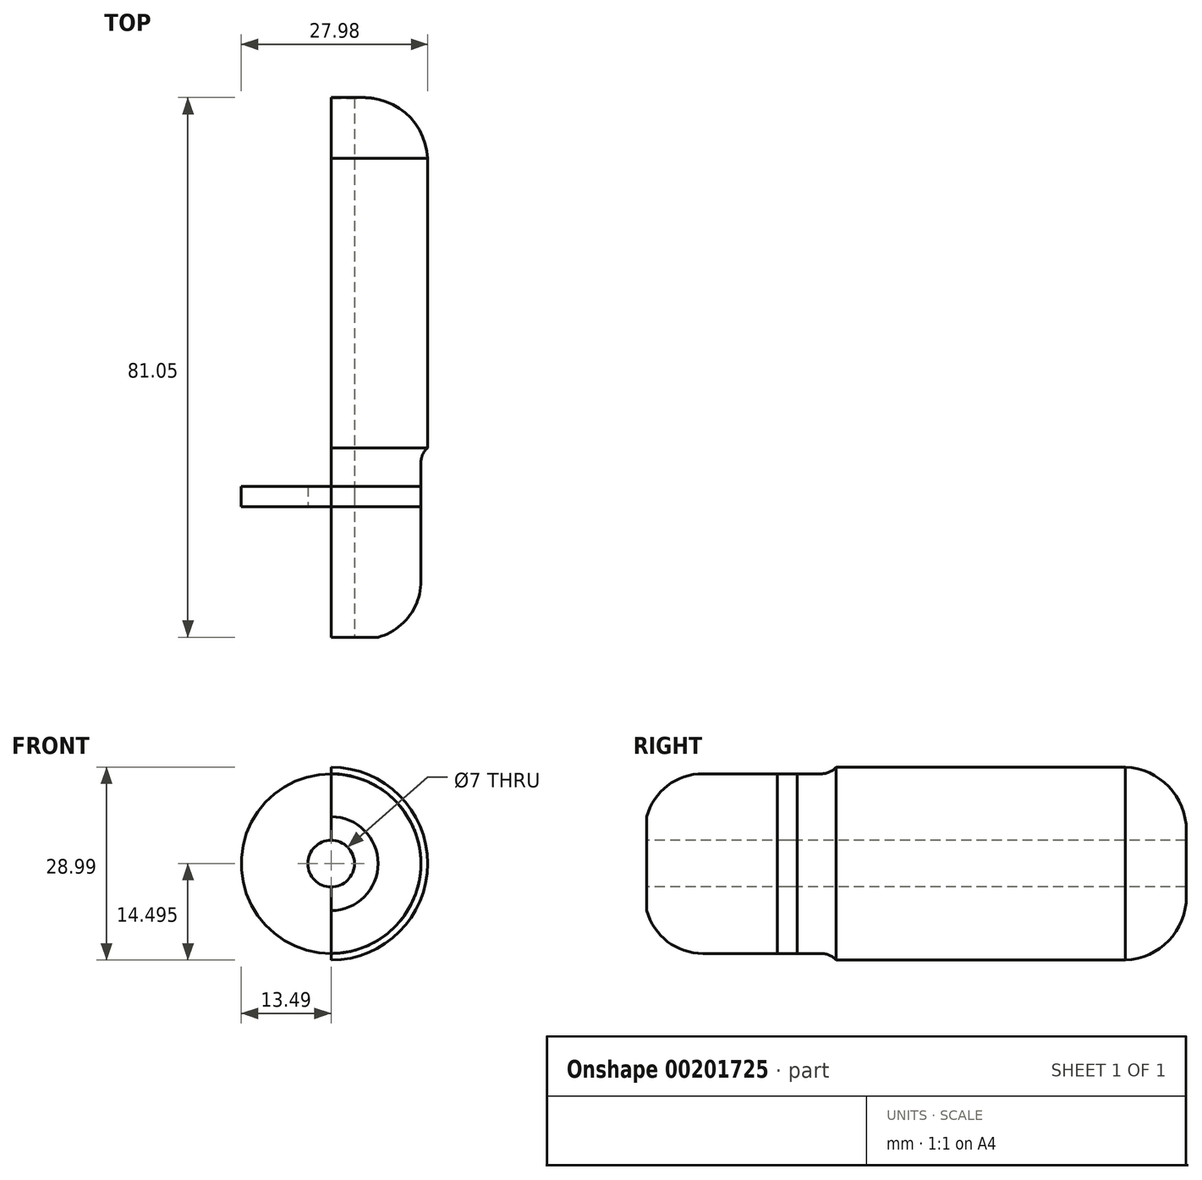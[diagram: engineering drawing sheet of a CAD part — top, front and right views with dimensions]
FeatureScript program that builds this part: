
annotation { "Feature Type Name" : "Feature", "Feature Type Description" : "" }
export const myFeature = defineFeature(function(context is Context, id is Id, definition is map)
    precondition{}
    {
        {
            var Q0;
            Q0=qCreatedBy(makeId("Right.planeOp"),FACE);
            var sketch = newSketch(context, id + "F0", { "sketchPlane" : qUnion([Q0])});
            skLineSegment(sketch, "E0.bottom", {"start": v(-3.13, 33.38) * mm, "end": v(86.87, 33.38) * mm});
            skLineSegment(sketch, "E0.top", {"start": v(-3.13, 32.38) * mm, "end": v(4.08, 32.38) * mm});
            skLineSegment(sketch, "E0.left", {"start": v(-3.13, 33.38) * mm, "end": v(-3.13, 32.38) * mm});
            skLineSegment(sketch, "E0.right", {"start": v(86.87, 33.38) * mm, "end": v(86.87, 32.38) * mm});
            skPoint(sketch, "E0.middle", {"position": v(41.87, 32.88) * mm});
            skLineSegment(sketch, "E1.bottom", {"start": v(86.87, 32.38) * mm, "end": v(81.87, 32.38) * mm, "construction": true});
            skLineSegment(sketch, "E1.top", {"start": v(86.87, 21.38) * mm, "end": v(85.87, 21.38) * mm});
            skLineSegment(sketch, "E1.left", {"start": v(86.87, 32.38) * mm, "end": v(86.87, 21.38) * mm, "construction": true});
            skLineSegment(sketch, "E1.right", {"start": v(81.87, 32.38) * mm, "end": v(81.87, 21.38) * mm, "construction": true});
            skLineSegment(sketch, "E2.bottom", {"start": v(81.87, 32.38) * mm, "end": v(71.87, 32.38) * mm, "construction": true});
            skLineSegment(sketch, "E2.top", {"start": v(81.87, 21.38) * mm, "end": v(71.87, 21.38) * mm, "construction": true});
            skLineSegment(sketch, "E2.right", {"start": v(71.87, 33.38) * mm, "end": v(71.87, 21.38) * mm, "construction": true});
            skLineSegment(sketch, "E3.0", {"start": v(85.87, 22.38) * mm, "end": v(85.37, 22.38) * mm, "construction": true});
            skLineSegment(sketch, "E4.0", {"start": v(85.87, 32.38) * mm, "end": v(85.87, 21.38) * mm, "construction": true});
            skArc(sketch, "E5", {"start": v(82.3, 22.38) * mm, "mid": v(80.84, 28.3) * mm, "end": v(76.33, 32.38) * mm});
            skArc(sketch, "E6", {"start": v(81.87, 21.38) * mm, "mid": v(79.3, 29.1) * mm, "end": v(71.87, 32.38) * mm});
            skLineSegment(sketch, "E7.trimOffspring", {"start": v(76.33, 32.38) * mm, "end": v(86.87, 32.38) * mm});
            skLineSegment(sketch, "E8.top", {"start": v(86.87, 25.38) * mm, "end": v(85.87, 25.38) * mm});
            skLineSegment(sketch, "E8.left", {"start": v(86.87, 23.38) * mm, "end": v(86.87, 25.38) * mm});
            skLineSegment(sketch, "E8.right", {"start": v(85.87, 22.38) * mm, "end": v(85.87, 22.72) * mm, "construction": true});
            skLineSegment(sketch, "E9.bottom", {"start": v(-3.13, 32.38) * mm, "end": v(-2.13, 32.38) * mm, "construction": true});
            skLineSegment(sketch, "E9.top", {"start": v(-3.13, 21.38) * mm, "end": v(-2.13, 21.38) * mm});
            skLineSegment(sketch, "E9.left", {"start": v(-3.13, 32.38) * mm, "end": v(-3.13, 21.38) * mm, "construction": true});
            skLineSegment(sketch, "E9.right", {"start": v(-2.13, 32.38) * mm, "end": v(-2.13, 21.38) * mm, "construction": true});
            skLineSegment(sketch, "E10.bottom", {"start": v(-2.13, 32.38) * mm, "end": v(4.08, 32.38) * mm, "construction": true});
            skLineSegment(sketch, "E10.top", {"start": v(-2.13, 33.38) * mm, "end": v(8.87, 33.38) * mm, "construction": true});
            skLineSegment(sketch, "E10.left", {"start": v(-2.13, 32.38) * mm, "end": v(-2.13, 33.38) * mm, "construction": true});
            skLineSegment(sketch, "E10.right", {"start": v(8.87, 32.38) * mm, "end": v(8.87, 33.38) * mm, "construction": true});
            skArc(sketch, "E11", {"start": v(4.08, 32.38) * mm, "mid": v(-1.17, 27.96) * mm, "end": v(-3.13, 21.38) * mm});
            skArc(sketch, "E12", {"start": v(8.87, 32.38) * mm, "mid": v(1.1, 29.16) * mm, "end": v(-2.13, 21.38) * mm});
            skLineSegment(sketch, "E13.trimOffspring", {"start": v(8.87, 32.38) * mm, "end": v(71.87, 32.38) * mm});
            skLineSegment(sketch, "E14", {"start": v(8.87, 21.38) * mm, "end": v(71.87, 21.38) * mm, "construction": true});
            skLineSegment(sketch, "E15.0", {"start": v(8.87, 17.38) * mm, "end": v(71.87, 17.38) * mm, "construction": true});
            skLineSegment(sketch, "E16.0", {"start": v(86.87, 23.38) * mm, "end": v(85.87, 23.38) * mm, "construction": true});
            skLineSegment(sketch, "E17.0", {"start": v(83.87, 21.38) * mm, "end": v(83.87, 25.38) * mm, "construction": true});
            skLineSegment(sketch, "E18", {"start": v(86.87, 23.38) * mm, "end": v(83.87, 21.38) * mm});
            skLineSegment(sketch, "E19.0", {"start": v(85.87, 23.92) * mm, "end": v(83.57, 22.38) * mm});
            skLineSegment(sketch, "E20.trimOffspring", {"start": v(83.87, 21.38) * mm, "end": v(81.87, 21.38) * mm});
            skLineSegment(sketch, "E21.trimOffspring", {"start": v(83.57, 22.38) * mm, "end": v(82.3, 22.38) * mm});
            skLineSegment(sketch, "E22.trimOffspring", {"start": v(85.87, 23.92) * mm, "end": v(85.87, 25.38) * mm});
            skSolve(sketch);
        }
        {
            var Q0;
            Q0=qCreatedBy(makeId("Right.planeOp"),FACE);
            var sketch = newSketch(context, id + "F1", { "sketchPlane" : qUnion([Q0])});
            skLineSegment(sketch, "E23.bottom", {"start": v(-3.13, 33.38) * mm, "end": v(28.58, 33.38) * mm, "construction": true});
            skLineSegment(sketch, "E23.left", {"start": v(-3.13, 33.38) * mm, "end": v(-3.13, 23.38) * mm, "construction": true});
            skLineSegment(sketch, "E23.right", {"start": v(28.58, 33.38) * mm, "end": v(28.58, 33.38) * mm});
            skLineSegment(sketch, "E24", {"start": v(28.58, 32.38) * mm, "end": v(8.84, 32.38) * mm, "construction": true});
            skArc(sketch, "E25", {"start": v(8.84, 32.38) * mm, "mid": v(1.84, 29.83) * mm, "end": v(-1.88, 23.38) * mm, "construction": true});
            skLineSegment(sketch, "E26.0", {"start": v(27.9, 31.88) * mm, "end": v(8.84, 31.88) * mm});
            skArc(sketch, "E27.0", {"start": v(8.84, 31.88) * mm, "mid": v(2.16, 29.45) * mm, "end": v(-1.38, 23.3) * mm});
            skLineSegment(sketch, "E28.0", {"start": v(26.58, 31.38) * mm, "end": v(8.84, 31.38) * mm});
            skArc(sketch, "E29.0", {"start": v(8.84, 30.88) * mm, "mid": v(2.9, 28.77) * mm, "end": v(-0.35, 23.38) * mm, "construction": true});
            skPoint(sketch, "E30.newPointB", {"position": v(28.58, 23.38) * mm});
            skArc(sketch, "E30.filletArc", {"start": v(26.58, 31.38) * mm, "mid": v(27.3, 31.5) * mm, "end": v(27.9, 31.88) * mm});
            skArc(sketch, "E31", {"start": v(8.84, 31.38) * mm, "mid": v(2.64, 29.01) * mm, "end": v(-0.4, 23.12) * mm});
            skLineSegment(sketch, "E32.trimOffspring", {"start": v(-1.37, 23.38) * mm, "end": v(-0.35, 23.38) * mm});
            skSolve(sketch);
        }
        {
            var Q0;
            Q0=qCreatedBy(makeId("Right.planeOp"),FACE);
            var sketch = newSketch(context, id + "F2", { "sketchPlane" : qUnion([Q0])});
            skLineSegment(sketch, "E33", {"start": v(86.87, 23.38) * mm, "end": v(83.87, 21.38) * mm, "construction": true});
            skLineSegment(sketch, "E34", {"start": v(83.87, 21.38) * mm, "end": v(81.87, 21.38) * mm, "construction": true});
            skLineSegment(sketch, "E35.0", {"start": v(86.87, 22.78) * mm, "end": v(84.02, 20.88) * mm});
            skLineSegment(sketch, "E36.0", {"start": v(84.02, 20.88) * mm, "end": v(81.87, 20.88) * mm});
            skLineSegment(sketch, "E37", {"start": v(86.87, 22.78) * mm, "end": v(86.87, 17.38) * mm});
            skLineSegment(sketch, "E38.0", {"start": v(66.87, 20.38) * mm, "end": v(66.87, 17.38) * mm});
            skLineSegment(sketch, "E39.0", {"start": v(81.87, 20.38) * mm, "end": v(66.87, 20.38) * mm});
            skLineSegment(sketch, "E40", {"start": v(71.87, 17.38) * mm, "end": v(66.87, 17.38) * mm});
            skLineSegment(sketch, "E41", {"start": v(71.87, 17.38) * mm, "end": v(86.87, 17.38) * mm});
            skLineSegment(sketch, "E42.0", {"start": v(81.87, 20.88) * mm, "end": v(81.87, 20.38) * mm});
            skSolve(sketch);
        }
        {
            var Q0;
            Q0=qCreatedBy(makeId("Right.planeOp"),FACE);
            var sketch = newSketch(context, id + "F3", { "sketchPlane" : qUnion([Q0])});
            skArc(sketch, "E43", {"start": v(81.87, 21.38) * mm, "mid": v(79.3, 29.1) * mm, "end": v(71.87, 32.38) * mm, "construction": true});
            skArc(sketch, "E44.0", {"start": v(81.3, 20.88) * mm, "mid": v(79.25, 28.4) * mm, "end": v(72.28, 31.88) * mm});
            skLineSegment(sketch, "E45", {"start": v(81.87, 20.38) * mm, "end": v(69.18, 20.38) * mm, "construction": true});
            skLineSegment(sketch, "E46", {"start": v(28.58, 32.38) * mm, "end": v(37.05, 32.38) * mm});
            skLineSegment(sketch, "E47", {"start": v(26.58, 31.38) * mm, "end": v(22.5, 31.38) * mm});
            skArc(sketch, "E48", {"start": v(26.58, 31.38) * mm, "mid": v(27.7, 31.64) * mm, "end": v(28.58, 32.38) * mm});
            skLineSegment(sketch, "E49.0", {"start": v(28.58, 31.88) * mm, "end": v(72.28, 31.88) * mm});
            skArc(sketch, "E50.0", {"start": v(26.58, 30.88) * mm, "mid": v(27.93, 31.2) * mm, "end": v(28.98, 32.08) * mm});
            skLineSegment(sketch, "E51.0", {"start": v(26.58, 30.88) * mm, "end": v(8.74, 30.88) * mm});
            skLineSegment(sketch, "E52.0", {"start": v(81.3, 20.88) * mm, "end": v(0.37, 20.88) * mm});
            skArc(sketch, "E53", {"start": v(8.84, 31.38) * mm, "mid": v(2.74, 29.11) * mm, "end": v(-0.35, 23.38) * mm, "construction": true});
            skArc(sketch, "E54.0", {"start": v(8.83, 30.88) * mm, "mid": v(3.5, 29.1) * mm, "end": v(0.37, 24.44) * mm});
            skLineSegment(sketch, "E55", {"start": v(-2.13, 27.58) * mm, "end": v(-2.13, 15.19) * mm, "construction": true});
            skLineSegment(sketch, "E56.trimOffspring", {"start": v(0.37, 24.44) * mm, "end": v(0.37, 20.88) * mm});
            skSolve(sketch);
        }
        {
            var Q0;
            Q0 = qSketchRegion(id + "F3", true);
            var Q1;
            Q1=sQuery(id+"F0.wireOp",EDGE,"E15.0");
            revolve(context, id + "F4", {"entities" : qUnion([Q0]), "axis" : qUnion([Q1]), "revolveType" : RevolveType.ONE_DIRECTION, "angle" : 180 * degree});
        }
        {
            var Q0;
            Q0 = qSketchRegion(id + "F3", true);
            var Q1;
            Q1=sQuery(id+"F0.wireOp",EDGE,"E15.0");
            revolve(context, id + "F5", {"entities" : qUnion([Q0]), "axis" : qUnion([Q1]), "revolveType" : RevolveType.FULL});
        }
        {
            var Q0;
            Q0=qCreatedBy(makeId("Front.planeOp"),FACE);
            var sketch = newSketch(context, id + "F6", { "sketchPlane" : qUnion([Q0])});
            skCircle(sketch, "E57", {"center": v(0, 17.38) * mm, "radius": 13.5 * mm});
            skSolve(sketch);
        }
        {
            var Q0;
            Q0=makeQuery(id+"F6.imprint","IMPRINT",FACE,{"disambiguationData":[TD([[makeQuery(id+"F6.imprint","IMPRINT",EDGE,{"derivedFrom":sQuery(id+"F6.wireOp",EDGE,"E57")}),1.0]])]});
            extrude(context, id + "F7", {"entities" : qUnion([Q0]), "oppositeDirection" : true, "depth" : 23 * mm, "hasSecondDirection" : true, "secondDirectionOppositeDirection" : true, "secondDirectionDepth" : 20 * mm});
        }
        {
            var Q0;
            Q0=makeQuery(id+"F5.opRevolve","SWEPT_BODY",BODY,{"disambiguationData":[OSD([sQuery(id+"F3.wireOp",EDGE,"E44.0"),sQuery(id+"F3.wireOp",EDGE,"E49.0"),sQuery(id+"F3.wireOp",EDGE,"E50.0"),sQuery(id+"F3.wireOp",EDGE,"E51.0"),sQuery(id+"F3.wireOp",EDGE,"E52.0"),sQuery(id+"F3.wireOp",EDGE,"E54.0"),sQuery(id+"F3.wireOp",EDGE,"E56.trimOffspring")])]});
            var Q1;
            Q1=makeQuery(id+"F7.opExtrude","SWEPT_BODY",BODY,{"disambiguationData":[OSD([sQuery(id+"F6.wireOp",EDGE,"E57")])]});
            booleanBodies(context, id + "F8", {"operationType" : BooleanOperationType.INTERSECTION, "tools" : qUnion([Q0, Q1])});
        }
    });
